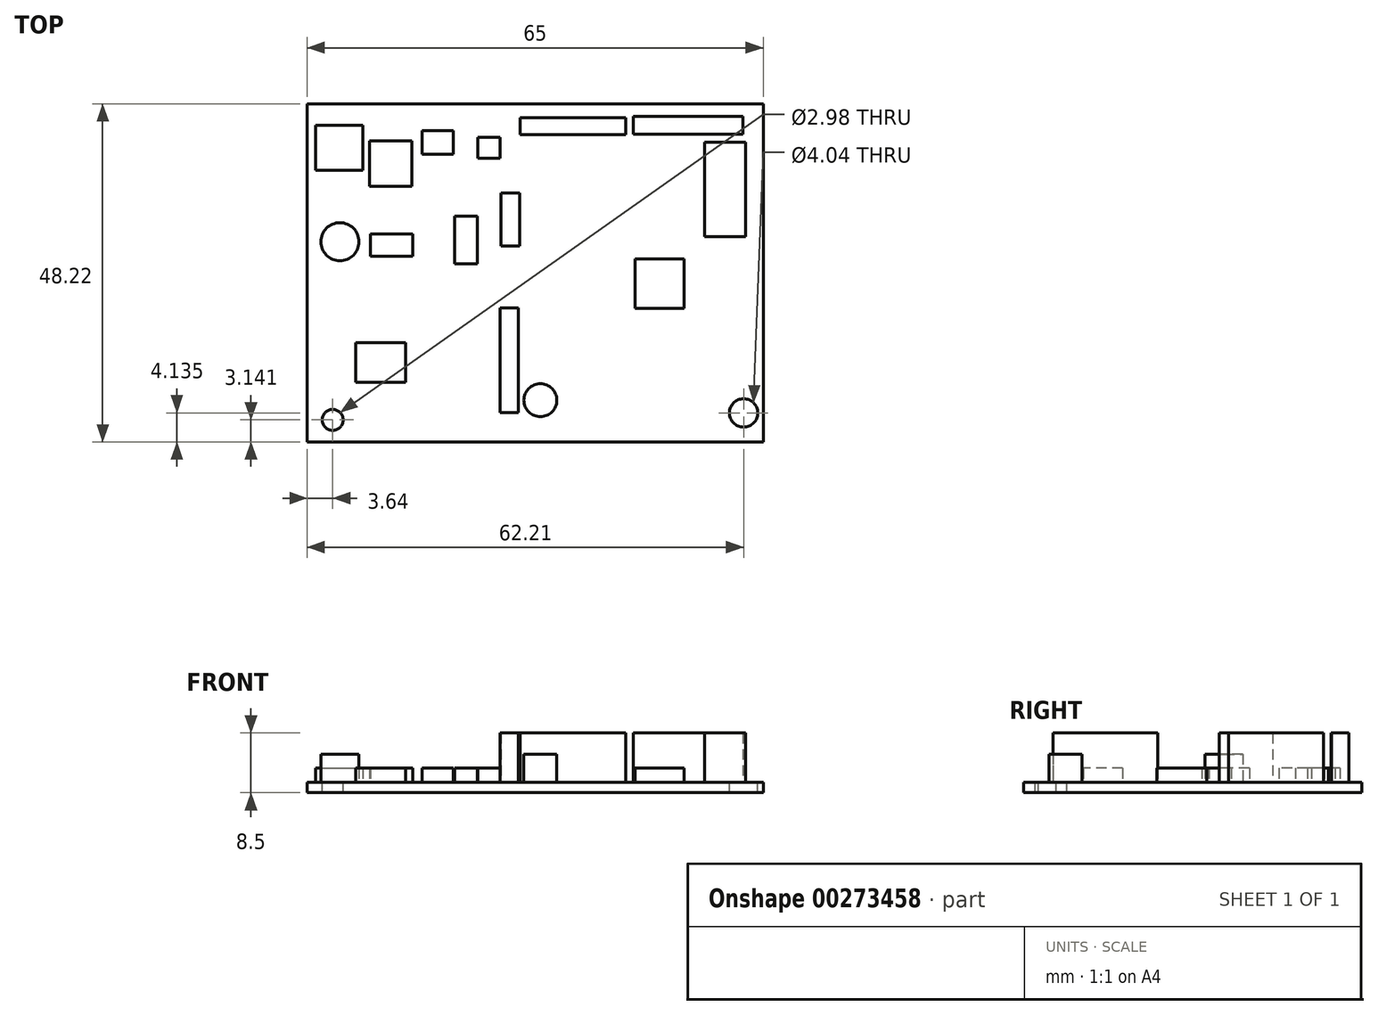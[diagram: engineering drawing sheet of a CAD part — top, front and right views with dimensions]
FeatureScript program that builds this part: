
annotation { "Feature Type Name" : "Feature", "Feature Type Description" : "" }
export const myFeature = defineFeature(function(context is Context, id is Id, definition is map)
    precondition{}
    {
        {
            var Q0;
            Q0=qCreatedBy(makeId("Top.planeOp"),FACE);
            var sketch = newSketch(context, id + "F0", { "sketchPlane" : qUnion([Q0])});
            skLineSegment(sketch, "E0", {"start": v(-16.18, -22.8) * mm, "end": v(-6.2, -22.34) * mm});
            skLineSegment(sketch, "E1.bottom", {"start": v(-17.13, 31.36) * mm, "end": v(47.87, 31.36) * mm});
            skLineSegment(sketch, "E1.top", {"start": v(-17.13, -16.86) * mm, "end": v(47.87, -16.86) * mm});
            skLineSegment(sketch, "E1.left", {"start": v(-17.13, 31.36) * mm, "end": v(-17.13, -16.86) * mm});
            skLineSegment(sketch, "E1.right", {"start": v(47.87, 31.36) * mm, "end": v(47.87, -16.86) * mm});
            skCircle(sketch, "E2", {"center": v(-13.5, -13.72) * mm, "radius": 1.5 * mm});
            skCircle(sketch, "E3", {"center": v(45.08, -12.72) * mm, "radius": 2.02 * mm});
            skLineSegment(sketch, "E4.bottom", {"start": v(-10.2, -2.73) * mm, "end": v(-3.08, -2.73) * mm});
            skLineSegment(sketch, "E4.top", {"start": v(-10.2, -8.36) * mm, "end": v(-3.08, -8.36) * mm});
            skLineSegment(sketch, "E4.left", {"start": v(-10.2, -2.73) * mm, "end": v(-10.2, -8.36) * mm});
            skLineSegment(sketch, "E4.right", {"start": v(-3.08, -2.73) * mm, "end": v(-3.08, -8.36) * mm});
            skLineSegment(sketch, "E5.bottom", {"start": v(-8.08, 12.76) * mm, "end": v(-2.09, 12.76) * mm});
            skLineSegment(sketch, "E5.top", {"start": v(-8.08, 9.6) * mm, "end": v(-2.09, 9.6) * mm});
            skLineSegment(sketch, "E5.left", {"start": v(-8.08, 12.76) * mm, "end": v(-8.08, 9.6) * mm});
            skLineSegment(sketch, "E5.right", {"start": v(-2.09, 12.76) * mm, "end": v(-2.09, 9.6) * mm});
            skLineSegment(sketch, "E6.bottom", {"start": v(3.9, 15.32) * mm, "end": v(7.13, 15.32) * mm});
            skLineSegment(sketch, "E6.top", {"start": v(3.9, 8.54) * mm, "end": v(7.13, 8.54) * mm});
            skLineSegment(sketch, "E6.left", {"start": v(3.9, 15.32) * mm, "end": v(3.9, 8.54) * mm});
            skLineSegment(sketch, "E6.right", {"start": v(7.13, 15.32) * mm, "end": v(7.13, 8.54) * mm});
            skLineSegment(sketch, "E7.bottom", {"start": v(-8.22, 26.04) * mm, "end": v(-2.19, 26.04) * mm});
            skLineSegment(sketch, "E7.top", {"start": v(-8.22, 19.56) * mm, "end": v(-2.19, 19.56) * mm});
            skLineSegment(sketch, "E7.left", {"start": v(-8.22, 26.04) * mm, "end": v(-8.22, 19.56) * mm});
            skLineSegment(sketch, "E7.right", {"start": v(-2.19, 26.04) * mm, "end": v(-2.19, 19.56) * mm});
            skLineSegment(sketch, "E8.bottom", {"start": v(-0.75, 27.53) * mm, "end": v(3.73, 27.53) * mm});
            skLineSegment(sketch, "E8.top", {"start": v(-0.75, 24.16) * mm, "end": v(3.73, 24.16) * mm});
            skLineSegment(sketch, "E8.left", {"start": v(-0.75, 27.53) * mm, "end": v(-0.75, 24.16) * mm});
            skLineSegment(sketch, "E8.right", {"start": v(3.73, 27.53) * mm, "end": v(3.73, 24.16) * mm});
            skLineSegment(sketch, "E9.bottom", {"start": v(7.22, 26.6) * mm, "end": v(10.38, 26.6) * mm});
            skLineSegment(sketch, "E9.top", {"start": v(7.22, 23.6) * mm, "end": v(10.38, 23.6) * mm});
            skLineSegment(sketch, "E9.left", {"start": v(7.22, 26.6) * mm, "end": v(7.22, 23.6) * mm});
            skLineSegment(sketch, "E9.right", {"start": v(10.38, 26.6) * mm, "end": v(10.38, 23.6) * mm});
            skLineSegment(sketch, "E10.bottom", {"start": v(-15.92, 28.25) * mm, "end": v(-9.22, 28.25) * mm});
            skLineSegment(sketch, "E10.top", {"start": v(-15.92, 21.89) * mm, "end": v(-9.22, 21.89) * mm});
            skLineSegment(sketch, "E10.left", {"start": v(-15.92, 28.25) * mm, "end": v(-15.92, 21.89) * mm});
            skLineSegment(sketch, "E10.right", {"start": v(-9.22, 28.25) * mm, "end": v(-9.22, 21.89) * mm});
            skLineSegment(sketch, "E11.bottom", {"start": v(29.64, 9.24) * mm, "end": v(36.6, 9.24) * mm});
            skLineSegment(sketch, "E11.top", {"start": v(29.64, 2.16) * mm, "end": v(36.6, 2.16) * mm});
            skLineSegment(sketch, "E11.left", {"start": v(29.64, 9.24) * mm, "end": v(29.64, 2.16) * mm});
            skLineSegment(sketch, "E11.right", {"start": v(36.6, 9.24) * mm, "end": v(36.6, 2.16) * mm});
            skCircle(sketch, "E12", {"center": v(16.11, -10.9) * mm, "radius": 2.35 * mm});
            skCircle(sketch, "E13", {"center": v(-12.45, 11.69) * mm, "radius": 2.71 * mm});
            skLineSegment(sketch, "E14.bottom", {"start": v(39.51, 25.9) * mm, "end": v(45.38, 25.9) * mm});
            skLineSegment(sketch, "E14.top", {"start": v(39.51, 12.38) * mm, "end": v(45.38, 12.38) * mm});
            skLineSegment(sketch, "E14.left", {"start": v(39.51, 25.9) * mm, "end": v(39.51, 12.38) * mm});
            skLineSegment(sketch, "E14.right", {"start": v(45.38, 25.9) * mm, "end": v(45.38, 12.38) * mm});
            skSolve(sketch);
        }
        {
            var Q0;
            Q0=makeQuery(id+"F0.imprint","IMPRINT",FACE,{"disambiguationData":[TD([[makeQuery(id+"F0.imprint","IMPRINT",EDGE,{"derivedFrom":sQuery(id+"F0.wireOp",EDGE,"E1.bottom")}),-1.0]])]});
            var Q1;
            Q1=makeQuery(id+"F0.imprint","IMPRINT",FACE,{"disambiguationData":[TD([[makeQuery(id+"F0.imprint","IMPRINT",EDGE,{"derivedFrom":sQuery(id+"F0.wireOp",EDGE,"E13")}),1.0]])]});
            var Q2;
            Q2=makeQuery(id+"F0.imprint","IMPRINT",FACE,{"disambiguationData":[TD([[makeQuery(id+"F0.imprint","IMPRINT",EDGE,{"derivedFrom":sQuery(id+"F0.wireOp",EDGE,"E4.bottom")}),-1.0]])]});
            var Q3;
            Q3=makeQuery(id+"F0.imprint","IMPRINT",FACE,{"disambiguationData":[TD([[makeQuery(id+"F0.imprint","IMPRINT",EDGE,{"derivedFrom":sQuery(id+"F0.wireOp",EDGE,"E5.bottom")}),-1.0]])]});
            var Q4;
            Q4=makeQuery(id+"F0.imprint","IMPRINT",FACE,{"disambiguationData":[TD([[makeQuery(id+"F0.imprint","IMPRINT",EDGE,{"derivedFrom":sQuery(id+"F0.wireOp",EDGE,"E7.bottom")}),-1.0]])]});
            var Q5;
            Q5=makeQuery(id+"F0.imprint","IMPRINT",FACE,{"disambiguationData":[TD([[makeQuery(id+"F0.imprint","IMPRINT",EDGE,{"derivedFrom":sQuery(id+"F0.wireOp",EDGE,"E10.bottom")}),-1.0]])]});
            var Q6;
            Q6=makeQuery(id+"F0.imprint","IMPRINT",FACE,{"disambiguationData":[TD([[makeQuery(id+"F0.imprint","IMPRINT",EDGE,{"derivedFrom":sQuery(id+"F0.wireOp",EDGE,"E8.bottom")}),-1.0]])]});
            var Q7;
            Q7=makeQuery(id+"F0.imprint","IMPRINT",FACE,{"disambiguationData":[TD([[makeQuery(id+"F0.imprint","IMPRINT",EDGE,{"derivedFrom":sQuery(id+"F0.wireOp",EDGE,"E6.bottom")}),-1.0]])]});
            var Q8;
            Q8=makeQuery(id+"F0.imprint","IMPRINT",FACE,{"disambiguationData":[TD([[makeQuery(id+"F0.imprint","IMPRINT",EDGE,{"derivedFrom":sQuery(id+"F0.wireOp",EDGE,"E9.bottom")}),-1.0]])]});
            var Q9;
            Q9=makeQuery(id+"F0.imprint","IMPRINT",FACE,{"disambiguationData":[TD([[makeQuery(id+"F0.imprint","IMPRINT",EDGE,{"derivedFrom":sQuery(id+"F0.wireOp",EDGE,"E12")}),1.0]])]});
            var Q10;
            Q10=makeQuery(id+"F0.imprint","IMPRINT",FACE,{"disambiguationData":[TD([[makeQuery(id+"F0.imprint","IMPRINT",EDGE,{"derivedFrom":sQuery(id+"F0.wireOp",EDGE,"E11.bottom")}),-1.0]])]});
            var Q11;
            Q11=makeQuery(id+"F0.imprint","IMPRINT",FACE,{"disambiguationData":[TD([[makeQuery(id+"F0.imprint","IMPRINT",EDGE,{"derivedFrom":sQuery(id+"F0.wireOp",EDGE,"E14.bottom")}),-1.0]])]});
            extrude(context, id + "F1", {"entities" : qUnion([Q0, Q1, Q2, Q3, Q4, Q5, Q6, Q7, Q8, Q9, Q10, Q11]), "oppositeDirection" : true, "depth" : 1.5 * mm});
        }
        {
            var Q0;
            Q0=makeQuery(id+"F0.imprint","IMPRINT",FACE,{"disambiguationData":[TD([[makeQuery(id+"F0.imprint","IMPRINT",EDGE,{"derivedFrom":sQuery(id+"F0.wireOp",EDGE,"E10.bottom")}),-1.0]])]});
            var Q1;
            Q1=makeQuery(id+"F0.imprint","IMPRINT",FACE,{"disambiguationData":[TD([[makeQuery(id+"F0.imprint","IMPRINT",EDGE,{"derivedFrom":sQuery(id+"F0.wireOp",EDGE,"E7.bottom")}),-1.0]])]});
            var Q2;
            Q2=makeQuery(id+"F0.imprint","IMPRINT",FACE,{"disambiguationData":[TD([[makeQuery(id+"F0.imprint","IMPRINT",EDGE,{"derivedFrom":sQuery(id+"F0.wireOp",EDGE,"E5.bottom")}),-1.0]])]});
            var Q3;
            Q3=makeQuery(id+"F0.imprint","IMPRINT",FACE,{"disambiguationData":[TD([[makeQuery(id+"F0.imprint","IMPRINT",EDGE,{"derivedFrom":sQuery(id+"F0.wireOp",EDGE,"E6.bottom")}),-1.0]])]});
            var Q4;
            Q4=makeQuery(id+"F0.imprint","IMPRINT",FACE,{"disambiguationData":[TD([[makeQuery(id+"F0.imprint","IMPRINT",EDGE,{"derivedFrom":sQuery(id+"F0.wireOp",EDGE,"E8.bottom")}),-1.0]])]});
            var Q5;
            Q5=makeQuery(id+"F0.imprint","IMPRINT",FACE,{"disambiguationData":[TD([[makeQuery(id+"F0.imprint","IMPRINT",EDGE,{"derivedFrom":sQuery(id+"F0.wireOp",EDGE,"E9.bottom")}),-1.0]])]});
            var Q6;
            Q6=makeQuery(id+"F0.imprint","IMPRINT",FACE,{"disambiguationData":[TD([[makeQuery(id+"F0.imprint","IMPRINT",EDGE,{"derivedFrom":sQuery(id+"F0.wireOp",EDGE,"E11.bottom")}),-1.0]])]});
            var Q7;
            Q7=makeQuery(id+"F0.imprint","IMPRINT",FACE,{"disambiguationData":[TD([[makeQuery(id+"F0.imprint","IMPRINT",EDGE,{"derivedFrom":sQuery(id+"F0.wireOp",EDGE,"E4.bottom")}),-1.0]])]});
            extrude(context, id + "F2", {"entities" : qUnion([Q0, Q1, Q2, Q3, Q4, Q5, Q6, Q7]), "operationType" : NewBodyOperationType.ADD, "depth" : 2 * mm});
        }
        {
            var Q0;
            Q0=makeQuery(id+"F0.imprint","IMPRINT",FACE,{"disambiguationData":[TD([[makeQuery(id+"F0.imprint","IMPRINT",EDGE,{"derivedFrom":sQuery(id+"F0.wireOp",EDGE,"E13")}),1.0]])]});
            var Q1;
            Q1=makeQuery(id+"F0.imprint","IMPRINT",FACE,{"disambiguationData":[TD([[makeQuery(id+"F0.imprint","IMPRINT",EDGE,{"derivedFrom":sQuery(id+"F0.wireOp",EDGE,"E12")}),1.0]])]});
            extrude(context, id + "F3", {"entities" : qUnion([Q0, Q1]), "operationType" : NewBodyOperationType.ADD, "depth" : 4 * mm});
        }
        {
            var Q0;
            Q0=makeQuery(id+"F0.imprint","IMPRINT",FACE,{"disambiguationData":[TD([[makeQuery(id+"F0.imprint","IMPRINT",EDGE,{"derivedFrom":sQuery(id+"F0.wireOp",EDGE,"E14.bottom")}),-1.0]])]});
            extrude(context, id + "F4", {"entities" : qUnion([Q0]), "operationType" : NewBodyOperationType.ADD, "depth" : 7 * mm});
        }
        {
            var Q0;
            Q0=makeQuery(id+"F0.imprint","IMPRINT",FACE,{"disambiguationData":[TD([[makeQuery(id+"F0.imprint","IMPRINT",EDGE,{"derivedFrom":sQuery(id+"F0.wireOp",EDGE,"E1.bottom")}),-1.0]])]});
            var sketch = newSketch(context, id + "F5", { "sketchPlane" : qUnion([Q0])});
            skLineSegment(sketch, "E15.bottom", {"start": v(13.24, 29.36) * mm, "end": v(28.27, 29.36) * mm});
            skLineSegment(sketch, "E15.top", {"start": v(13.24, 26.94) * mm, "end": v(28.27, 26.94) * mm});
            skLineSegment(sketch, "E15.left", {"start": v(13.24, 29.36) * mm, "end": v(13.24, 26.94) * mm});
            skLineSegment(sketch, "E15.right", {"start": v(28.27, 29.36) * mm, "end": v(28.27, 26.94) * mm});
            skLineSegment(sketch, "E16.bottom", {"start": v(29.37, 29.52) * mm, "end": v(44.95, 29.52) * mm});
            skLineSegment(sketch, "E16.top", {"start": v(29.37, 27.02) * mm, "end": v(44.95, 27.02) * mm});
            skLineSegment(sketch, "E16.left", {"start": v(29.37, 29.52) * mm, "end": v(29.37, 27.02) * mm});
            skLineSegment(sketch, "E16.right", {"start": v(44.95, 29.52) * mm, "end": v(44.95, 27.02) * mm});
            skLineSegment(sketch, "E17.bottom", {"start": v(10.5, 18.64) * mm, "end": v(13.17, 18.64) * mm});
            skLineSegment(sketch, "E17.top", {"start": v(10.5, 11.05) * mm, "end": v(13.17, 11.05) * mm});
            skLineSegment(sketch, "E17.left", {"start": v(10.5, 18.64) * mm, "end": v(10.5, 11.05) * mm});
            skLineSegment(sketch, "E17.right", {"start": v(13.17, 18.64) * mm, "end": v(13.17, 11.05) * mm});
            skLineSegment(sketch, "E18.bottom", {"start": v(10.38, 2.24) * mm, "end": v(12.99, 2.24) * mm});
            skLineSegment(sketch, "E18.top", {"start": v(10.38, -12.65) * mm, "end": v(12.99, -12.65) * mm});
            skLineSegment(sketch, "E18.left", {"start": v(10.38, 2.24) * mm, "end": v(10.38, -12.65) * mm});
            skLineSegment(sketch, "E18.right", {"start": v(12.99, 2.24) * mm, "end": v(12.99, -12.65) * mm});
            skLineSegment(sketch, "E19.bottom", {"start": v(21.55, -3.44) * mm, "end": v(29.19, -3.44) * mm});
            skLineSegment(sketch, "E19.top", {"start": v(21.55, -5.58) * mm, "end": v(29.19, -5.58) * mm});
            skLineSegment(sketch, "E19.left", {"start": v(21.55, -3.44) * mm, "end": v(21.55, -5.58) * mm});
            skLineSegment(sketch, "E19.right", {"start": v(29.19, -3.44) * mm, "end": v(29.19, -5.58) * mm});
            skSolve(sketch);
        }
        {
            var Q0;
            Q0=makeQuery(id+"F5.imprint","IMPRINT",FACE,{"disambiguationData":[TD([[makeQuery(id+"F5.imprint","IMPRINT",EDGE,{"derivedFrom":sQuery(id+"F5.wireOp",EDGE,"E18.bottom")}),-1.0]])]});
            var Q1;
            Q1=makeQuery(id+"F5.imprint","IMPRINT",FACE,{"disambiguationData":[TD([[makeQuery(id+"F5.imprint","IMPRINT",EDGE,{"derivedFrom":sQuery(id+"F5.wireOp",EDGE,"E17.bottom")}),-1.0]])]});
            var Q2;
            Q2=makeQuery(id+"F5.imprint","IMPRINT",FACE,{"disambiguationData":[TD([[makeQuery(id+"F5.imprint","IMPRINT",EDGE,{"derivedFrom":sQuery(id+"F5.wireOp",EDGE,"E15.bottom")}),-1.0]])]});
            var Q3;
            Q3=makeQuery(id+"F5.imprint","IMPRINT",FACE,{"disambiguationData":[TD([[makeQuery(id+"F5.imprint","IMPRINT",EDGE,{"derivedFrom":sQuery(id+"F5.wireOp",EDGE,"E16.bottom")}),-1.0]])]});
            extrude(context, id + "F6", {"entities" : qUnion([Q0, Q1, Q2, Q3]), "operationType" : NewBodyOperationType.ADD, "depth" : 7 * mm});
        }
    });
